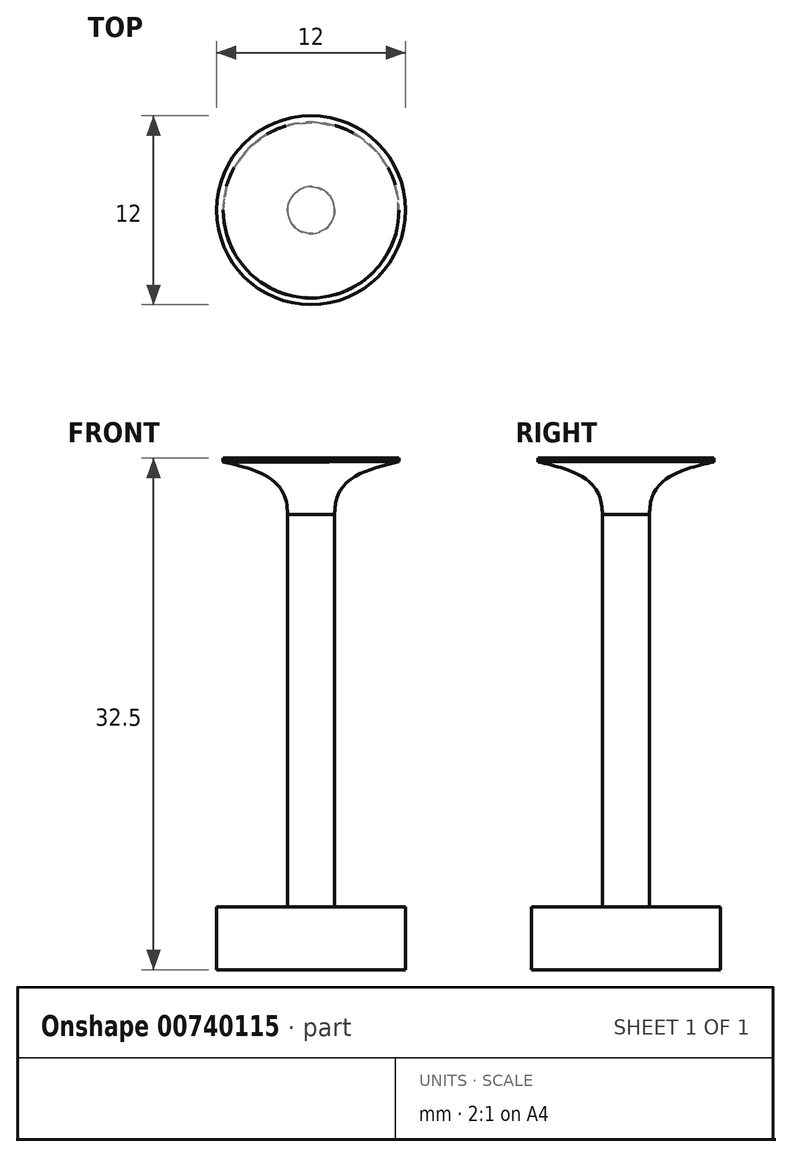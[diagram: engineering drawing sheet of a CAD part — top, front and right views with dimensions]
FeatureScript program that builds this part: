
annotation { "Feature Type Name" : "Feature", "Feature Type Description" : "" }
export const myFeature = defineFeature(function(context is Context, id is Id, definition is map)
    precondition{}
    {
        {
            var Q0;
            Q0=qCreatedBy(makeId("Front.planeOp"),FACE);
            var sketch = newSketch(context, id + "F0", { "sketchPlane" : qUnion([Q0])});
            skPoint(sketch, "E0.0", {"position": v(1.87, 2.88) * mm});
            skFitSpline(sketch, "E1.0", {"points": [v(-3.2, 2.88) * mm, v(-0.93, 2.88) * mm, v(1.34, 2.88) * mm, v(3.6, 2.88) * mm]});
            skLineSegment(sketch, "E2", {"start": v(1.87, -6.62) * mm, "end": v(0.37, -6.62) * mm});
            skFitSpline(sketch, "E3", {"points": [v(-3.72, 2.88) * mm, v(-3.72, 2.7) * mm, v(-3.72, 2.65) * mm, v(-2.38, 2.05) * mm, v(-1.08, 1.33) * mm, v(-0.04, 0.05) * mm, v(0.37, -0.68) * mm, v(0.37, -0.71) * mm], "startDerivative": vector(0.18, -2.66) * mm, "endDerivative": vector(-0.17, -1.01) * mm});
            skLineSegment(sketch, "E4", {"start": v(0.38, -0.7) * mm, "end": v(0.37, -6.62) * mm});
            skLineSegment(sketch, "E5", {"start": v(1.87, -6.62) * mm, "end": v(1.87, 2.88) * mm});
            skLineSegment(sketch, "E6", {"start": v(-3.72, 2.88) * mm, "end": v(1.87, 2.88) * mm});
            skLineSegment(sketch, "E7", {"start": v(-3.72, 2.88) * mm, "end": v(-3.71, 2.65) * mm});
            skFitSpline(sketch, "E8", {"points": [v(0.38, -0.7) * mm, v(0.17, 0.54) * mm, v(-0.95, 1.73) * mm, v(-3.71, 2.65) * mm], "startDerivative": vector(-0.23, 4.62) * mm, "endDerivative": vector(-7.37, 1.76) * mm});
            skLineSegment(sketch, "E9", {"start": v(1.87, 2.88) * mm, "end": v(1.87, 3.38) * mm});
            skLineSegment(sketch, "E10", {"start": v(1.87, 3.38) * mm, "end": v(-3.72, 3.38) * mm});
            skLineSegment(sketch, "E11", {"start": v(-3.72, 3.38) * mm, "end": v(-3.72, 2.88) * mm});
            skSolve(sketch);
        }
        {
            var Q0;
            Q0=makeQuery(id+"F0.imprint","IMPRINT",FACE,{"disambiguationData":[TD([[makeQuery(id+"F0.imprint","IMPRINT",EDGE,{"derivedFrom":sQuery(id+"F0.wireOp",EDGE,"E2")}),-1.0]])]});
            var Q1;
            Q1=sQuery(id+"F0.wireOp",EDGE,"E5");
            revolve(context, id + "F1", {"surfaceOperationType" : NewSurfaceOperationType.NEW, "entities" : qUnion([Q0]), "axis" : qUnion([Q1]), "revolveType" : RevolveType.FULL});
        }
        {
            var Q0;
            Q0=qCreatedBy(makeId("Top.planeOp"),FACE);
            var sketch = newSketch(context, id + "F2", { "sketchPlane" : qUnion([Q0])});
            skCircle(sketch, "E12", {"center": v(1.87, 0) * mm, "radius": 1.5 * mm});
            skSolve(sketch);
        }
        {
            var Q0;
            Q0 = qSketchRegion(id + "F2", true);
            extrude(context, id + "F3", {"entities" : qUnion([Q0]), "operationType" : NewBodyOperationType.ADD, "oppositeDirection" : true, "depth" : 50 * mm, "offsetDistance" : 25 * mm});
        }
        {
            var Q0;
            Q0=qCreatedBy(makeId("Front.planeOp"),FACE);
            var sketch = newSketch(context, id + "F4", { "sketchPlane" : qUnion([Q0])});
            skPoint(sketch, "E13.0", {"position": v(1.87, 2.88) * mm});
            skFitSpline(sketch, "E14.0", {"points": [v(0.38, -0.7) * mm, v(0.38, -0.7) * mm, v(0.45, -0.7) * mm, v(0.79, -0.7) * mm, v(1.28, -0.7) * mm, v(1.87, -0.7) * mm, v(2.46, -0.7) * mm, v(2.96, -0.7) * mm, v(3.3, -0.7) * mm, v(3.37, -0.7) * mm, v(3.37, -0.7) * mm]});
            skLineSegment(sketch, "E15.0", {"start": v(3.37, -6.62) * mm, "end": v(0.37, -6.62) * mm});
            skLineSegment(sketch, "E16", {"start": v(1.87, 2.88) * mm, "end": v(1.87, -5.62) * mm, "construction": true});
            skLineSegment(sketch, "E17", {"start": v(1.87, -5.62) * mm, "end": v(1.87, -25.62) * mm, "construction": true});
            skSolve(sketch);
        }
        {
            var Q0;
            Q0=sQuery(id+"F4.wireOp",VERTEX,"E17.end");
            var Q1;
            Q1=qCreatedBy(makeId("Top.planeOp"),FACE);
            cPlane(context, id + "F5", {"entities" : qUnion([Q0, Q1]), "cplaneType" : CPlaneType.PLANE_POINT, "offset" : 25 * mm, "width" : 150 * mm, "height" : 150 * mm});
        }
        {
            var Q0;
            Q0=qCreatedBy(id+"F5.planeOp",FACE);
            var sketch = newSketch(context, id + "F6", { "sketchPlane" : qUnion([Q0])});
            skLineSegment(sketch, "E18.bottom", {"start": v(-20.6, -36.4) * mm, "end": v(39.61, -36.4) * mm});
            skLineSegment(sketch, "E18.top", {"start": v(-20.6, 43.88) * mm, "end": v(39.61, 43.88) * mm});
            skLineSegment(sketch, "E18.left", {"start": v(-20.6, -36.4) * mm, "end": v(-20.6, 43.88) * mm});
            skLineSegment(sketch, "E18.right", {"start": v(39.61, -36.4) * mm, "end": v(39.61, 43.88) * mm});
            skSolve(sketch);
        }
        {
            var Q0;
            Q0=makeQuery(id+"F6.imprint","IMPRINT",FACE,{"disambiguationData":[TD([[makeQuery(id+"F6.imprint","IMPRINT",EDGE,{"derivedFrom":sQuery(id+"F6.wireOp",EDGE,"E18.bottom")}),1.0]])]});
            extrude(context, id + "F7", {"entities" : qUnion([Q0]), "operationType" : NewBodyOperationType.REMOVE, "oppositeDirection" : true, "depth" : 78.3 * mm, "offsetDistance" : 25 * mm});
        }
        {
            var Q0;
            Q0=qCreatedBy(id+"F5.planeOp",FACE);
            var sketch = newSketch(context, id + "F8", { "sketchPlane" : qUnion([Q0])});
            skPoint(sketch, "E19.0", {"position": v(1.87, 0) * mm});
            skCircle(sketch, "E20", {"center": v(1.87, 0) * mm, "radius": 6 * mm});
            skSolve(sketch);
        }
        {
            var Q0;
            Q0=makeQuery(id+"F8.imprint","IMPRINT",FACE,{"disambiguationData":[TD([[makeQuery(id+"F8.imprint","IMPRINT",EDGE,{"derivedFrom":sQuery(id+"F8.wireOp",EDGE,"E20")}),1.0]])]});
            extrude(context, id + "F9", {"entities" : qUnion([Q0]), "operationType" : NewBodyOperationType.ADD, "oppositeDirection" : true, "depth" : 4 * mm, "offsetDistance" : 25 * mm});
        }
    });
